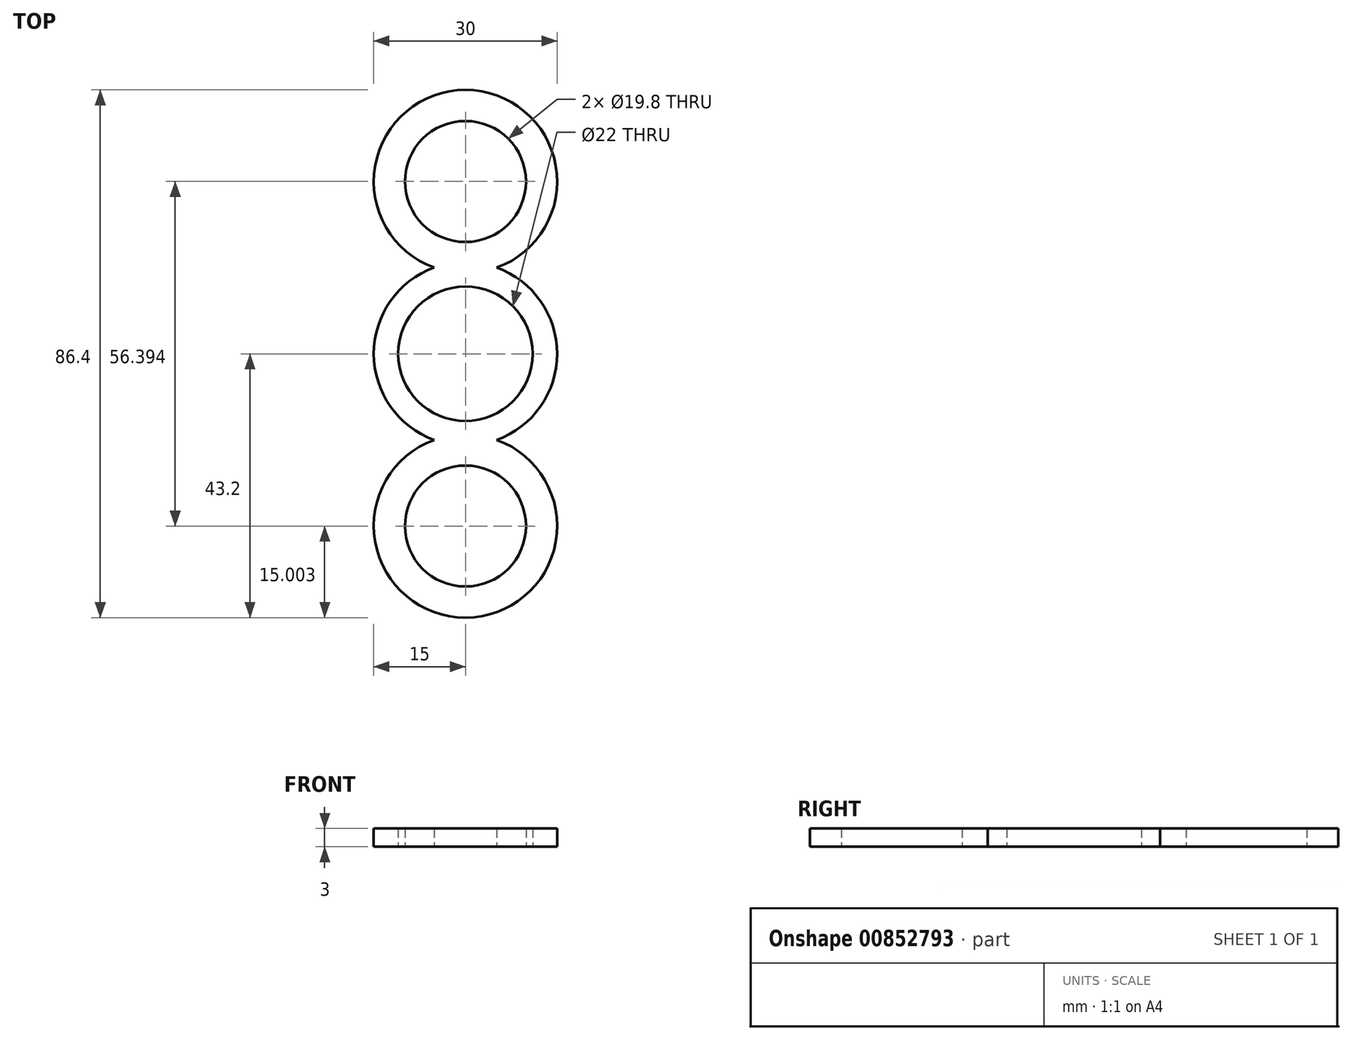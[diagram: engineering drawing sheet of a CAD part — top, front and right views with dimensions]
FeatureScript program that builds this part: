
annotation { "Feature Type Name" : "Feature", "Feature Type Description" : "" }
export const myFeature = defineFeature(function(context is Context, id is Id, definition is map)
    precondition{}
    {
        {
            var Q0;
            Q0=qCreatedBy(makeId("Top.planeOp"),FACE);
            var sketch = newSketch(context, id + "F0", { "sketchPlane" : qUnion([Q0])});
            skCircle(sketch, "E0", {"center": v(0, 0) * mm, "radius": 11 * mm});
            skArc(sketch, "E1", {"start": v(-5.12, 14.1) * mm, "mid": v(-15, 0) * mm, "end": v(-5.12, -14.1) * mm});
            skCircle(sketch, "E2", {"center": v(0, 28.2) * mm, "radius": 9.9 * mm});
            skArc(sketch, "E3", {"start": v(5.12, 14.1) * mm, "mid": v(0, 43.2) * mm, "end": v(-5.12, 14.1) * mm});
            skCircle(sketch, "E4", {"center": v(0, -28.2) * mm, "radius": 9.9 * mm});
            skArc(sketch, "E5", {"start": v(-5.12, -14.1) * mm, "mid": v(0, -43.2) * mm, "end": v(5.12, -14.1) * mm});
            skArc(sketch, "E6.trimOffspring", {"start": v(5.12, -14.1) * mm, "mid": v(15, 0) * mm, "end": v(5.12, 14.1) * mm});
            skSolve(sketch);
        }
        {
            var Q0;
            Q0=qSketchRegion(id+"F0",true);
            extrude(context, id + "F1", {"entities" : qUnion([Q0]), "depth" : 3 * mm, "offsetDistance" : 25 * mm});
        }
    });
